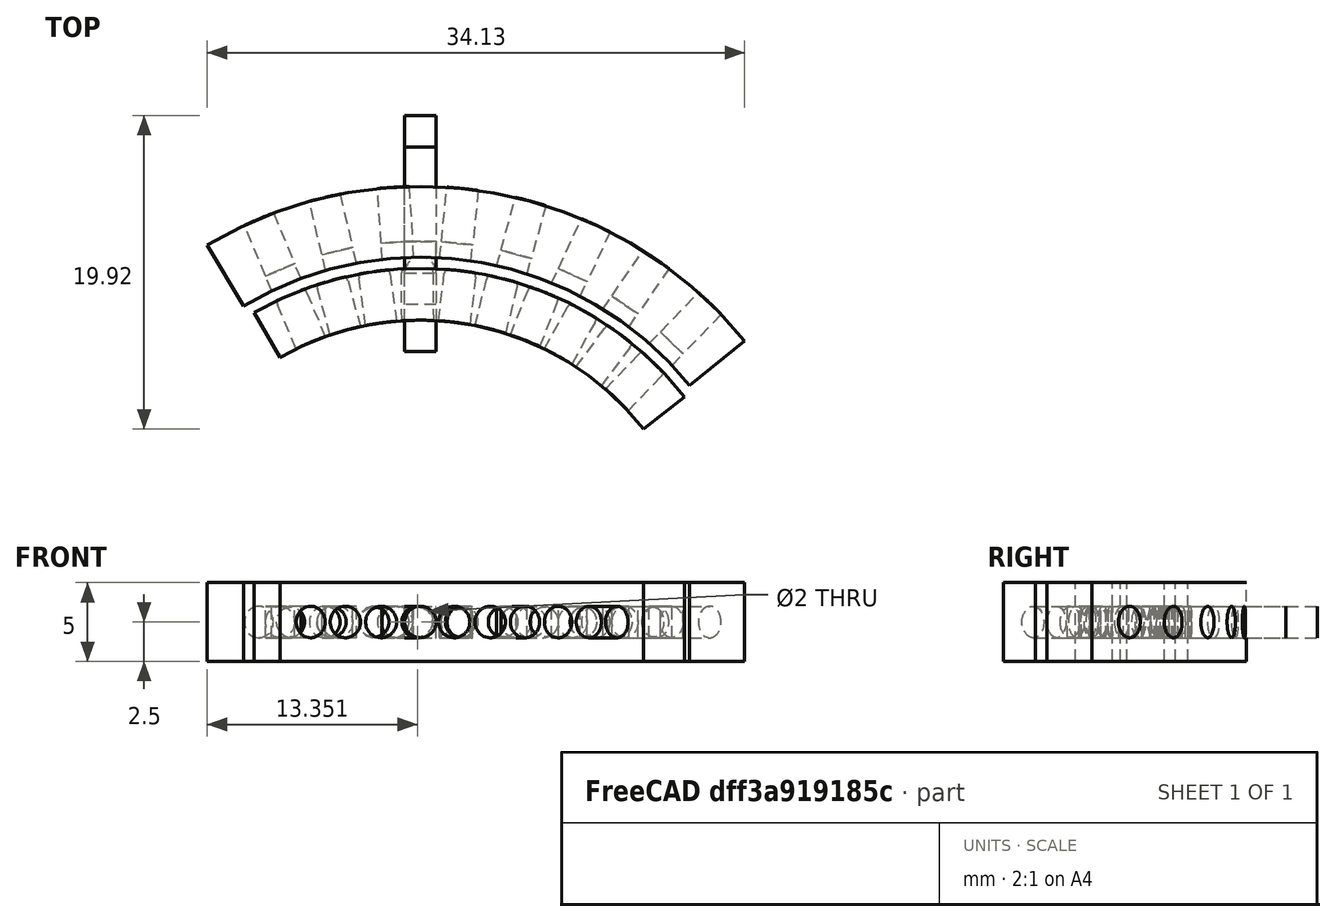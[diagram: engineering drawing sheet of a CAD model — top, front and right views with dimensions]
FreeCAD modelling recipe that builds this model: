
FCSTD DOCUMENT  (FreeCAD 0.21R33771 (Git))
Label: F_macro_ring
License: All rights reserved
LicenseURL: http://en.wikipedia.org/wiki/All_rights_reserved
objects: Part::Cylinder×5, Part::FeaturePython×5, App::Part×3, Mesh::Feature×2, Part::Sphere×2, Part::MultiFuse×2, Part::MultiCommon×2, Part::Cut×2, Sketcher::SketchObject×1, PartDesign::Body×1, Spreadsheet::Sheet×1, Image::ImagePlane×1, Part::Box×1, Part::Fuse×1
note: 19 computed .brp shape members not serialized (recipe doc carries the construction recipe); baked Part::Feature solids carry a one-line shape summary decoded from their .brp

FEATURE [Mesh::Feature] _0mm_macro_nikon_b  label="40mm_macro_nikon_b"
FEATURE [Sketcher::SketchObject] Sketch
  FullyConstrained = true
  MapMode = 5
  Support = -> [XY_Plane]
  expr: Constraints[1] = <<Spreadsheet>>.ContactMidRadius
  sketch-geometry (1):
    g0: Circle CenterX=0 CenterY=0 CenterZ=0 NormalX=0 NormalY=0 NormalZ=1 AngleXU=0 Radius=22
  constraints (2):
    c: Coincident(g0,g-1)
    c: Radius(g0) = 22
FEATURE [PartDesign::Body] Body
  Group = -> [Sketch]
  Origin = -> Origin
FEATURE [Spreadsheet::Sheet] Spreadsheet
  cells = A1='ContactMidRadius; B1(ContactMidRadius)==22 mm; E1='Lens Contact max contact distance; F1==2.42 cm; G1==2.42 cm; A2='ContactGirth; B2(ContactGirth)==1.5 mm; E2='Body Contact max contact distance; F2==2.42 cm; A3='LensContact_Spacing; B3(LensContact_Spacing)==1 mm; A4='BodyContact_Side; B4(BodyContact_Side)==2 mm; F4==F1 / 2 / B4; A5='BodyContact_Spacing; B5(BodyContact_Spacing)==1 mm; A6='BodyContact_PinNumber; B6(BodyContact_PinNumber)=8; A7='LensContact _PinNumber_SmolZoom; B7(LensContact__PinNumber_SmolZoom)=10; A8='BodyContact_Angle; B8(BodyContact_Angle)==asin(F2 / 2 / B1) * 2; C8='LensContact_Angle; D8(LensContact_Angle)==asin(F1 / 2 / B1) * 2; A9='BodyContact_Diameter; B9(BodyContact_Diameter)==sqrt(BodyContact_Side / 2 * BodyContact_Side / 2 + BodyContact_Side / 2 * BodyContact_Side / 2); A10='WireGap; B10==0.25 mm
FEATURE [Part::Cylinder] Cylinder  label="Contact"
  Angle = 360
  AttacherType = Attacher::AttachEngine3D
  FirstAngle = 0
  Height = 7
  Placement = pos=(0,29,1) rot=(1,0,0;1.5708rad)
  Radius = 1
  SecondAngle = 0
  expr: .Placement.Base.y = <<Spreadsheet>>.ContactMidRadius + Height
  expr: .Placement.Base.z = <<Spreadsheet>>.BodyContact_Side / 2
  expr: Radius = <<Spreadsheet>>.BodyContact_Side / 2
FEATURE [Image::ImagePlane] Nikon_F_mount_mechDwg  label="Nikon_F-mount_mechDwg"
  Placement = pos=(9,-3.5,4e-16) rot=(1,0,0;3.14159rad)
  XSize = 106.081
  YSize = 129.274
FEATURE [Part::Box] Box  label="Cube"
  AttacherType = Attacher::AttachEngine3D
  Height = 2
  Length = 2
  Placement = pos=(-1,21,0) rot=(0,0,1;0rad)
  Width = 2
  expr: .Placement.Base.x = -<<Spreadsheet>>.BodyContact_Side / 2
  expr: .Placement.Base.y = <<Spreadsheet>>.ContactMidRadius - <<Spreadsheet>>.BodyContact_Side / 2
  expr: Height = <<Spreadsheet>>.BodyContact_Side
  expr: Length = <<Spreadsheet>>.BodyContact_Side
  expr: Width = <<Spreadsheet>>.BodyContact_Side
FEATURE [Part::Fuse] Fusion
  Base = -> Cylinder
  Tool = -> Box
FEATURE [Part::FeaturePython] Array  label="BodySide_Contacts"  # Draft array (typed FeaturePython)
  AlwaysSyncPlacement = false
  Angle = -66.734
  ArrayType = 1
  Axis = (0,0,1)
  Base = -> Fusion
  Center = (0,0,0)
  Count = 8
  ExpandArray = false
  Fuse = false
  IntervalAxis = (0,0,0)
  IntervalX = (50,0,0)
  IntervalY = (0,50,0)
  IntervalZ = (0,0,50)
  NumberCircles = 3
  NumberPolar = 8
  NumberX = 2
  NumberY = 2
  NumberZ = 1
  Placement = pos=(0,0,0) rot=(0,0,1;0.397935rad)
  PlacementList = 8 placements: [(0,0,0),(0,0,0),(0,0,0),(0,0,0),(0,0,0),(0,0,0),(0,0,0),(0,0,0)]
  RadialDistance = 50
  ScaleList = (8) [(1,1,1),(1,1,1),(1,1,1),(1,1,1),(1,1,1),(1,1,1),(1,1,1),(1,1,1)]
  Symmetry = 1
  TangentialDistance = 25
  expr: Angle = -<<Spreadsheet>>.BodyContact_Angle
FEATURE [Part::Cylinder] Cylinder001  label="Contact001"
  Angle = 360
  AttacherType = Attacher::AttachEngine3D
  FirstAngle = 0
  Height = 5
  Placement = pos=(0,21,1) rot=(1,0,0;1.5708rad)
  Radius = 1
  SecondAngle = 0
  expr: .Placement.Base.y = <<Spreadsheet>>.ContactMidRadius - <<Spreadsheet>>.BodyContact_Side / 2
  expr: .Placement.Base.z = <<Spreadsheet>>.BodyContact_Side / 2
  expr: Height = 5 mm
  expr: Radius = <<Spreadsheet>>.BodyContact_Side / 2
FEATURE [Part::Sphere] Sphere
  Angle1 = -90
  Angle2 = 90
  Angle3 = 360
  AttacherType = Attacher::AttachEngine3D
  Placement = pos=(0,21,1) rot=(0,0,1;0rad)
  Radius = 1
  expr: .Placement.Base.y = <<Spreadsheet>>.ContactMidRadius - <<Spreadsheet>>.BodyContact_Side / 2
  expr: .Placement.Base.z = <<Spreadsheet>>.BodyContact_Side / 2
  expr: Radius = <<Spreadsheet>>.BodyContact_Side / 2
FEATURE [Part::MultiFuse] Fusion001
  Shapes = -> [Sphere,Cylinder001]
FEATURE [Part::FeaturePython] Array001  label="LensSideContacts"  # Draft array (typed FeaturePython)
  AlwaysSyncPlacement = false
  Angle = -66.734
  ArrayType = 1
  Axis = (0,0,1)
  Base = -> Fusion001
  Center = (0,0,0)
  Count = 10
  ExpandArray = false
  Fuse = false
  IntervalAxis = (0,0,0)
  IntervalX = (50,0,0)
  IntervalY = (0,50,0)
  IntervalZ = (0,0,50)
  NumberCircles = 3
  NumberPolar = 10
  NumberX = 2
  NumberY = 2
  NumberZ = 1
  Placement = pos=(0,0,0) rot=(0,0,1;0.397935rad)
  PlacementList = 10 placements: [(0,0,0),(0,0,0),(0,0,0),(0,0,0),(0,0,0),(0,0,0),(0,0,0),(0,0,0),(0,0,0),(0,0,0)]
  RadialDistance = 50
  ScaleList = (10) [(1,1,1),(1,1,1),(1,1,1),(1,1,1),(1,1,1),(1,1,1),(1,1,1),(1,1,1),(1,1,1),(1,1,1)]
  Symmetry = 1
  TangentialDistance = 25
  expr: Angle = -<<Spreadsheet>>.LensContact_Angle
  expr: NumberPolar = 10
FEATURE [Part::FeaturePython] Tube  # WARN: FeaturePython — macro-defined, semantics opaque (R4)
  AttacherType = Attacher::AttachEngine3D
  Height = 5
  InnerRadius = 18
  OuterRadius = 21.2929
  Placement = pos=(0,0,-1.5) rot=(0,0,1;0rad)
  expr: InnerRadius = <<Spreadsheet>>.ContactMidRadius - 4 mm
  expr: OuterRadius = <<Spreadsheet>>.ContactMidRadius - <<Spreadsheet>>.BodyContact_Diameter / 2
FEATURE [Part::Cylinder] Cylinder002  label="Cylinder"
  Angle = 81.734
  AttacherType = Attacher::AttachEngine3D
  FirstAngle = 0
  Height = 10
  Placement = pos=(0,0,-3) rot=(0,0,1;0.785398rad)
  Radius = 32
  SecondAngle = 0
  expr: Angle = <<Spreadsheet>>.LensContact_Angle + 15 °
FEATURE [Part::MultiCommon] Common
  Placement = pos=(0,0,0) rot=(0,0,-1;0.122173rad)
  Shapes = -> [Tube,Cylinder002]
FEATURE [Part::Cut] Cut
  Base = -> Common
  Tool = -> Array001
FEATURE [Part::FeaturePython] Tube001  # WARN: FeaturePython — macro-defined, semantics opaque (R4)
  AttacherType = Attacher::AttachEngine3D
  Height = 5
  InnerRadius = 22
  OuterRadius = 26.5
  Placement = pos=(0,0,-1.5) rot=(0,0,1;0rad)
  expr: InnerRadius = <<Spreadsheet>>.ContactMidRadius
  expr: OuterRadius = <<Spreadsheet>>.ContactMidRadius + 4.5 mm
FEATURE [Part::Cylinder] Cylinder003
  Angle = 81.734
  AttacherType = Attacher::AttachEngine3D
  FirstAngle = 0
  Height = 10
  Placement = pos=(0,0,-3) rot=(0,0,1;0.750492rad)
  Radius = 27
  SecondAngle = 0
  expr: .Placement.Rotation.Angle = 43 °
  expr: Angle = <<Spreadsheet>>.BodyContact_Angle + 15 °
  expr: Radius = <<Spreadsheet>>.ContactMidRadius + 5 mm
FEATURE [Part::MultiCommon] Common001
  Placement = pos=(0,0,0) rot=(0,0,-1;0.069813rad)
  Shapes = -> [Cylinder003,Tube001]
FEATURE [Part::Cut] Cut001
  Base = -> Common001
  Tool = -> Array
FEATURE [App::Part] Part  label="Body_side_contact_bracket"
  Group = -> [Cylinder003,Tube001,Common001,Cylinder,Array,Box,Fusion,Cut001]
  Origin = -> Origin001
  Placement = pos=(0,0,5) rot=(0,0,1;0rad)
FEATURE [App::Part] Part001  label="Lens_side_contact_bracket"
  Group = -> [Tube,Common,Cylinder002,Array001,Cylinder001,Sphere,Fusion001,Cut]
  Origin = -> Origin002
  Placement = pos=(0,0,41.5) rot=(0,0,1;0rad)
FEATURE [Part::Cylinder] Cylinder004  label="Contact002"
  Angle = 360
  AttacherType = Attacher::AttachEngine3D
  FirstAngle = 0
  Height = 12
  Placement = pos=(0,31,1) rot=(1,0,0;1.5708rad)
  Radius = 1
  SecondAngle = 0
  expr: .Placement.Base.y = <<Spreadsheet>>.ContactMidRadius - <<Spreadsheet>>.BodyContact_Side / 2 + 10 mm
  expr: .Placement.Base.z = <<Spreadsheet>>.BodyContact_Side / 2
  expr: Radius = <<Spreadsheet>>.BodyContact_Side / 2
FEATURE [Part::Sphere] Sphere001
  Angle1 = -90
  Angle2 = 90
  Angle3 = 360
  AttacherType = Attacher::AttachEngine3D
  Placement = pos=(0,21,1) rot=(0,0,1;0rad)
  Radius = 1
  expr: .Placement.Base.y = <<Spreadsheet>>.ContactMidRadius - <<Spreadsheet>>.BodyContact_Side / 2
  expr: .Placement.Base.z = <<Spreadsheet>>.BodyContact_Side / 2
  expr: Radius = <<Spreadsheet>>.BodyContact_Side / 2
FEATURE [Part::MultiFuse] Fusion002
  Shapes = -> [Sphere001,Cylinder004]
FEATURE [Part::FeaturePython] Array002  label="LensSideContacts001"  # Draft array (typed FeaturePython)
  AlwaysSyncPlacement = false
  Angle = -66.734
  ArrayType = 1
  Axis = (0,0,1)
  Base = -> Fusion002
  Center = (0,0,0)
  Count = 10
  ExpandArray = false
  Fuse = false
  IntervalAxis = (0,0,0)
  IntervalX = (50,0,0)
  IntervalY = (0,50,0)
  IntervalZ = (0,0,50)
  NumberCircles = 3
  NumberPolar = 10
  NumberX = 2
  NumberY = 2
  NumberZ = 1
  Placement = pos=(0,0,0) rot=(0,0,1;0.397935rad)
  PlacementList = 10 placements: [(0,0,0),(0,0,0),(0,0,0),(0,0,0),(0,0,0),(0,0,0),(0,0,0),(0,0,0),(0,0,0),(0,0,0)]
  RadialDistance = 50
  ScaleList = (10) [(1,1,1),(1,1,1),(1,1,1),(1,1,1),(1,1,1),(1,1,1),(1,1,1),(1,1,1),(1,1,1),(1,1,1)]
  Symmetry = 1
  TangentialDistance = 25
  expr: Angle = -<<Spreadsheet>>.LensContact_Angle
  expr: NumberPolar = 10
FEATURE [App::Part] Part002  label="Out_traces"
  Group = -> [Fusion002,Sphere001,Cylinder004,Array002]
  Origin = -> Origin003
  Placement = pos=(0,0,29) rot=(0,0,1;0rad)
FEATURE [Mesh::Feature] Difference003
